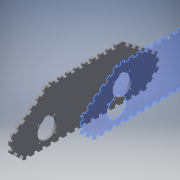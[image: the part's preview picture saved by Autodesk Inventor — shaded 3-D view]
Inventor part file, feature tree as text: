
AUTODESK INVENTOR PART (.ipt)
format: ipt  version: 2019 (Build 230136000, 136)  size: 392,704 bytes
history: native  units: mm
features: reference x20, other x6, sketch x3, extrude x2
ambient origin geometry x8: Origin, YZ Plane, XZ Plane, XY Plane, X Axis, Y Axis, Z Axis, Center Point
bodies: Body1 (feature_tree)
feature tree (31):
  other  "Твердое тело1"
  extrude  "Выдавливание1"  Depth=67.0mm
  sketch  "Эскиз2"
  extrude  "Выдавливание2"  Depth=50.0mm
  sketch  "Эскиз1"
  reference  "Ссылка1"
  reference  "Ссылка2"
  reference  "Ссылка3"
  reference  "Ссылка4"
  reference  "Ссылка5"
  reference  "Ссылка6"
  reference  "Ссылка7"
  reference  "Ссылка8"
  reference  "Ссылка9"
  reference  "Ссылка10"
  reference  "Ссылка11"
  reference  "Ссылка12"
  reference  "Ссылка13"
  reference  "Ссылка14"
  reference  "Ссылка15"
  reference  "Ссылка16"
  reference  "Ссылка17"
  reference  "Ссылка18"
  reference  "Ссылка19"
  reference  "Ссылка20"
  sketch  "Эскиз3"
  other  "Сборка2"
  other  "Моторный блок:1"
  other  "mot37:1"
  other  "Моторный блок:2"
  other  "Диск.0001:1"
